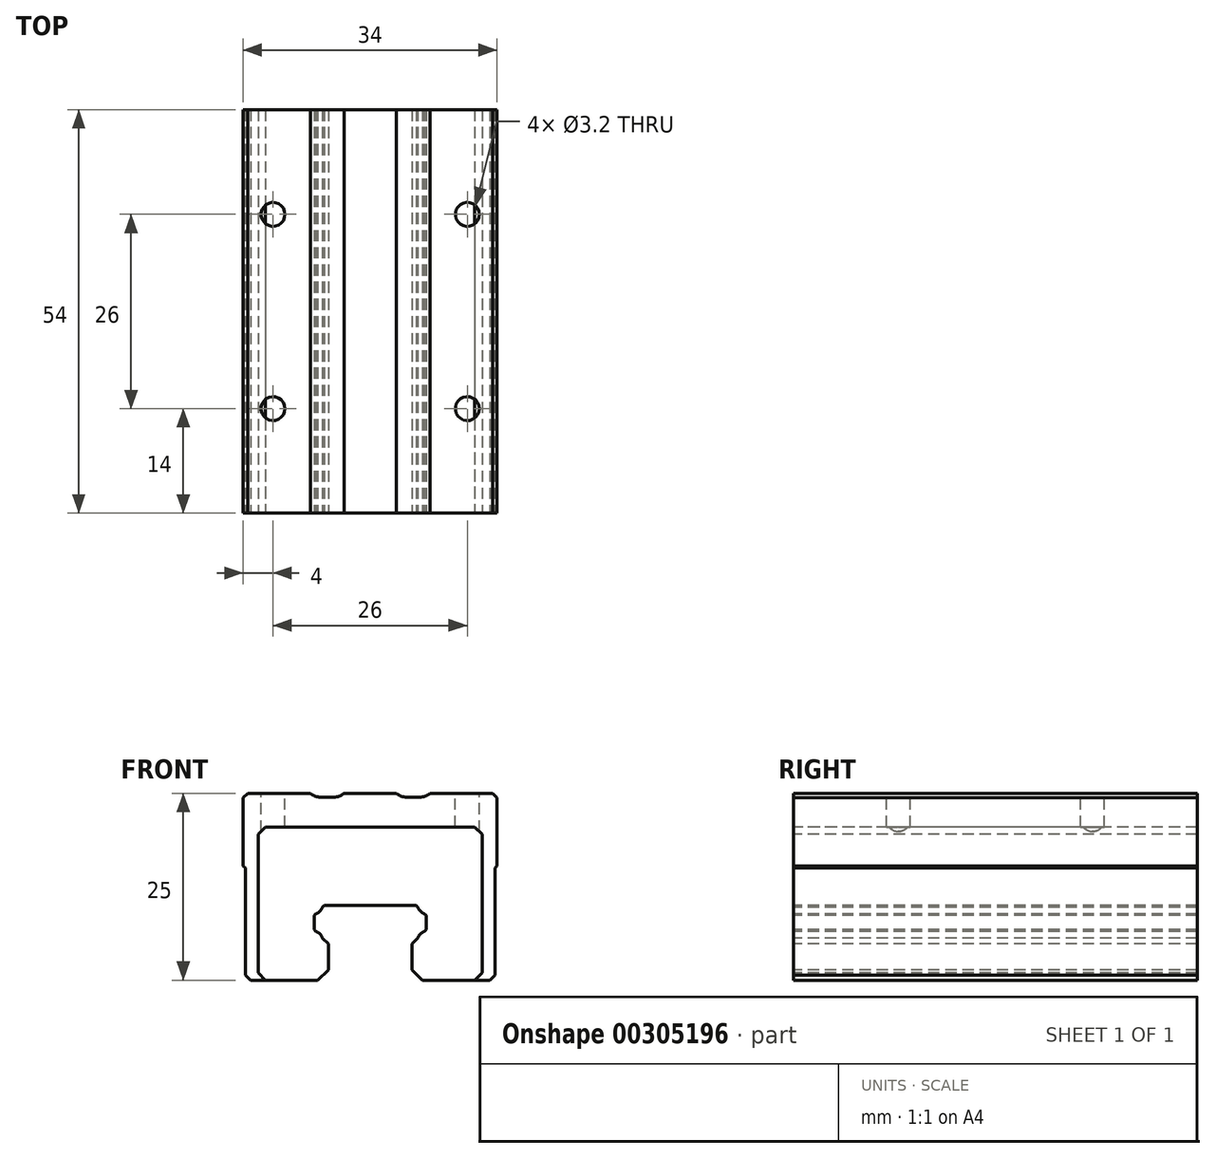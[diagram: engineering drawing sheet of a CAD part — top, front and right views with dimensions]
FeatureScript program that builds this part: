
annotation { "Feature Type Name" : "Feature", "Feature Type Description" : "" }
export const myFeature = defineFeature(function(context is Context, id is Id, definition is map)
    precondition{}
    {
        {
            var Q0;
            Q0=qCreatedBy(makeId("Front.planeOp"),FACE);
            var sketch = newSketch(context, id + "F0", { "sketchPlane" : qUnion([Q0])});
            skLineSegment(sketch, "E0.0", {"start": v(-7, -11.09) * mm, "end": v(-14, -11.09) * mm});
            skLineSegment(sketch, "E1.0", {"start": v(-14, -11.09) * mm, "end": v(-16, -11.09) * mm});
            skLineSegment(sketch, "E2.0", {"start": v(-16, -11.09) * mm, "end": v(-16.7, -10.39) * mm});
            skLineSegment(sketch, "E3.0", {"start": v(-16.7, -10.39) * mm, "end": v(-16.7, 3.91) * mm});
            skLineSegment(sketch, "E4.0", {"start": v(-17, 4.21) * mm, "end": v(-17, 13.31) * mm});
            skLineSegment(sketch, "E5.0", {"start": v(-16.7, 3.91) * mm, "end": v(-17, 4.21) * mm});
            skLineSegment(sketch, "E6.0", {"start": v(-17, 13.31) * mm, "end": v(-16.4, 13.91) * mm});
            skLineSegment(sketch, "E7.0", {"start": v(-16.4, 13.91) * mm, "end": v(-8, 13.91) * mm});
            skArc(sketch, "E8.0", {"start": v(-8, 13.91) * mm, "mid": v(-7.38, 13.54) * mm, "end": v(-6.67, 13.41) * mm});
            skLineSegment(sketch, "E9.0", {"start": v(-6.67, 13.41) * mm, "end": v(-4.83, 13.41) * mm});
            skArc(sketch, "E10.0", {"start": v(-4.83, 13.41) * mm, "mid": v(-4.12, 13.54) * mm, "end": v(-3.5, 13.91) * mm});
            skLineSegment(sketch, "E11.0", {"start": v(-3.5, 13.91) * mm, "end": v(3.5, 13.91) * mm});
            skArc(sketch, "E12.0", {"start": v(3.5, 13.91) * mm, "mid": v(4.12, 13.54) * mm, "end": v(4.83, 13.41) * mm});
            skLineSegment(sketch, "E13.0", {"start": v(4.83, 13.41) * mm, "end": v(6.67, 13.41) * mm});
            skArc(sketch, "E14.0", {"start": v(6.67, 13.41) * mm, "mid": v(7.38, 13.54) * mm, "end": v(8, 13.91) * mm});
            skLineSegment(sketch, "E15.0", {"start": v(8, 13.91) * mm, "end": v(16.4, 13.91) * mm});
            skLineSegment(sketch, "E16.0", {"start": v(16.4, 13.91) * mm, "end": v(17, 13.31) * mm});
            skLineSegment(sketch, "E17.0", {"start": v(17, 13.31) * mm, "end": v(17, 4.21) * mm});
            skLineSegment(sketch, "E18.0", {"start": v(17, 4.21) * mm, "end": v(16.7, 3.91) * mm});
            skLineSegment(sketch, "E19.0", {"start": v(16.7, 3.91) * mm, "end": v(16.7, -10.39) * mm});
            skLineSegment(sketch, "E20.0", {"start": v(16.7, -10.39) * mm, "end": v(16, -11.09) * mm});
            skLineSegment(sketch, "E21.0", {"start": v(16, -11.09) * mm, "end": v(14, -11.09) * mm});
            skLineSegment(sketch, "E22.0", {"start": v(14, -11.09) * mm, "end": v(7, -11.09) * mm});
            skLineSegment(sketch, "E23.0.0", {"start": v(-7, -11.09) * mm, "end": v(-5.6, -9.69) * mm});
            skLineSegment(sketch, "E23.0.1", {"start": v(-5.6, -9.69) * mm, "end": v(-5.6, -6.24) * mm});
            skLineSegment(sketch, "E23.0.2", {"start": v(-5.6, -6.24) * mm, "end": v(-6.37, -5.47) * mm});
            skArc(sketch, "E23.0.3", {"start": v(-6.37, -5.47) * mm, "mid": v(-6.72, -4.9) * mm, "end": v(-7.28, -4.55) * mm});
            skLineSegment(sketch, "E23.0.4", {"start": v(-7.28, -4.55) * mm, "end": v(-7.5, -4.34) * mm});
            skLineSegment(sketch, "E23.0.5", {"start": v(-7.5, -4.34) * mm, "end": v(-7.5, -2.44) * mm});
            skLineSegment(sketch, "E23.0.6", {"start": v(-7.5, -2.44) * mm, "end": v(-7.28, -2.22) * mm});
            skArc(sketch, "E23.0.7", {"start": v(-7.28, -2.22) * mm, "mid": v(-6.72, -1.87) * mm, "end": v(-6.37, -1.3) * mm});
            skLineSegment(sketch, "E23.0.8", {"start": v(-6.37, -1.3) * mm, "end": v(-6.15, -1.09) * mm});
            skLineSegment(sketch, "E23.0.9", {"start": v(-6.15, -1.09) * mm, "end": v(6.15, -1.09) * mm});
            skLineSegment(sketch, "E23.0.10", {"start": v(6.15, -1.09) * mm, "end": v(6.37, -1.3) * mm});
            skArc(sketch, "E23.0.11", {"start": v(6.37, -1.3) * mm, "mid": v(6.72, -1.87) * mm, "end": v(7.28, -2.22) * mm});
            skLineSegment(sketch, "E23.0.12", {"start": v(7.28, -2.22) * mm, "end": v(7.5, -2.44) * mm});
            skLineSegment(sketch, "E23.0.13", {"start": v(7.5, -2.44) * mm, "end": v(7.5, -4.34) * mm});
            skLineSegment(sketch, "E23.0.14", {"start": v(7.5, -4.34) * mm, "end": v(7.28, -4.55) * mm});
            skArc(sketch, "E23.0.15", {"start": v(7.28, -4.55) * mm, "mid": v(6.72, -4.9) * mm, "end": v(6.37, -5.47) * mm});
            skLineSegment(sketch, "E23.0.16", {"start": v(6.37, -5.47) * mm, "end": v(5.6, -6.24) * mm});
            skLineSegment(sketch, "E23.0.17", {"start": v(5.6, -6.24) * mm, "end": v(5.6, -9.69) * mm});
            skLineSegment(sketch, "E23.0.18", {"start": v(5.6, -9.69) * mm, "end": v(7, -11.09) * mm});
            skLineSegment(sketch, "E23.0.19", {"start": v(7, -11.09) * mm, "end": v(14, -11.09) * mm});
            skLineSegment(sketch, "E23.0.20", {"start": v(14, -11.09) * mm, "end": v(15, -10.09) * mm});
            skLineSegment(sketch, "E23.0.21", {"start": v(15, -10.09) * mm, "end": v(15, 8.41) * mm});
            skLineSegment(sketch, "E23.0.22", {"start": v(15, 8.41) * mm, "end": v(14, 9.41) * mm});
            skLineSegment(sketch, "E23.0.23", {"start": v(14, 9.41) * mm, "end": v(-14, 9.41) * mm});
            skLineSegment(sketch, "E23.0.24", {"start": v(-14, 9.41) * mm, "end": v(-15, 8.41) * mm});
            skLineSegment(sketch, "E23.0.25", {"start": v(-15, 8.41) * mm, "end": v(-15, -10.09) * mm});
            skLineSegment(sketch, "E23.0.26", {"start": v(-15, -10.09) * mm, "end": v(-14, -11.09) * mm});
            skLineSegment(sketch, "E23.0.27", {"start": v(-14, -11.09) * mm, "end": v(-7, -11.09) * mm});
            skSolve(sketch);
        }
        {
            var Q0;
            Q0=makeQuery(id+"F0.imprint","IMPRINT",FACE,{"disambiguationData":[TD([[makeQuery(id+"F0.imprint","IMPRINT",EDGE,{"derivedFrom":sQuery(id+"F0.wireOp",EDGE,"E1.0")}),-1.0]])]});
            extrude(context, id + "F1", {"entities" : qUnion([Q0]), "oppositeDirection" : true, "depth" : 54 * mm});
        }
        {
            var Q0;
            Q0=makeQuery(id+"F0.imprint","IMPRINT",FACE,{"disambiguationData":[TD([[makeQuery(id+"F0.imprint","IMPRINT",EDGE,{"derivedFrom":sQuery(id+"F0.wireOp",EDGE,"E23.0.0")}),1.0]])]});
            extrude(context, id + "F2", {"entities" : qUnion([Q0]), "oppositeDirection" : true, "depth" : 54 * mm});
        }
        {
            var Q0;
            Q0=makeQuery(id+"F1.opExtrude","SWEPT_FACE",FACE,{"disambiguationData":[OSD([sQuery(id+"F0.wireOp",EDGE,"E7.0")])]});
            var sketch = newSketch(context, id + "F3", { "sketchPlane" : qUnion([Q0])});
            skPoint(sketch, "E24", {"position": v(-13, 40) * mm});
            skPoint(sketch, "E25", {"position": v(13, 40) * mm});
            skPoint(sketch, "E26", {"position": v(13, 14) * mm});
            skPoint(sketch, "E27", {"position": v(-13, 14) * mm});
            skSolve(sketch);
        }
        {
            var Q0;
            Q0=sQuery(id+"F3.wireOp",VERTEX,"E26");
            var Q1;
            Q1=sQuery(id+"F3.wireOp",VERTEX,"E27");
            var Q2;
            Q2=sQuery(id+"F3.wireOp",VERTEX,"E24");
            var Q3;
            Q3=sQuery(id+"F3.wireOp",VERTEX,"E25");
            var Q4;
            Q4=makeQuery(id+"F1.opExtrude","SWEPT_BODY",BODY,{"disambiguationData":[OSD([sQuery(id+"F0.wireOp",EDGE,"E1.0"),sQuery(id+"F0.wireOp",EDGE,"E2.0"),sQuery(id+"F0.wireOp",EDGE,"E3.0"),sQuery(id+"F0.wireOp",EDGE,"E4.0"),sQuery(id+"F0.wireOp",EDGE,"E5.0"),sQuery(id+"F0.wireOp",EDGE,"E6.0"),sQuery(id+"F0.wireOp",EDGE,"E7.0"),sQuery(id+"F0.wireOp",EDGE,"E8.0"),sQuery(id+"F0.wireOp",EDGE,"E9.0"),sQuery(id+"F0.wireOp",EDGE,"E10.0"),sQuery(id+"F0.wireOp",EDGE,"E11.0"),sQuery(id+"F0.wireOp",EDGE,"E12.0"),sQuery(id+"F0.wireOp",EDGE,"E13.0"),sQuery(id+"F0.wireOp",EDGE,"E14.0"),sQuery(id+"F0.wireOp",EDGE,"E15.0"),sQuery(id+"F0.wireOp",EDGE,"E16.0"),sQuery(id+"F0.wireOp",EDGE,"E17.0"),sQuery(id+"F0.wireOp",EDGE,"E18.0"),sQuery(id+"F0.wireOp",EDGE,"E19.0"),sQuery(id+"F0.wireOp",EDGE,"E20.0"),sQuery(id+"F0.wireOp",EDGE,"E21.0"),sQuery(id+"F0.wireOp",EDGE,"E23.0.20"),sQuery(id+"F0.wireOp",EDGE,"E23.0.21"),sQuery(id+"F0.wireOp",EDGE,"E23.0.22"),sQuery(id+"F0.wireOp",EDGE,"E23.0.23"),sQuery(id+"F0.wireOp",EDGE,"E23.0.24"),sQuery(id+"F0.wireOp",EDGE,"E23.0.25"),sQuery(id+"F0.wireOp",EDGE,"E23.0.26")])]});
            hole(context, id + "F4", {"style" : HoleStyle.SIMPLE, "endStyle" : HoleEndStyle.BLIND, "standardTappedOrClearance" : lookupTablePath({ "standard" : "ISO", "engagement" : "75%", "pitch" : "0.75 mm", "size" : "M4", "type" : "Tapped" }), "standardBlindInLast" : lookupTablePath({ "standard" : "ISO", "engagement" : "75%", "pitch" : "0.75 mm", "size" : "M4", "type" : "Tapped" }), "holeDiameter" : 3.2 * mm, "showTappedDepth" : true, "holeDepth" : 14.25 * mm, "tappedDepth" : 12 * mm, "tapClearance" : 3, "startFromSketch" : true, "locations" : qUnion([Q0, Q1, Q2, Q3]), "scope" : qUnion([Q4])});
        }
    });
